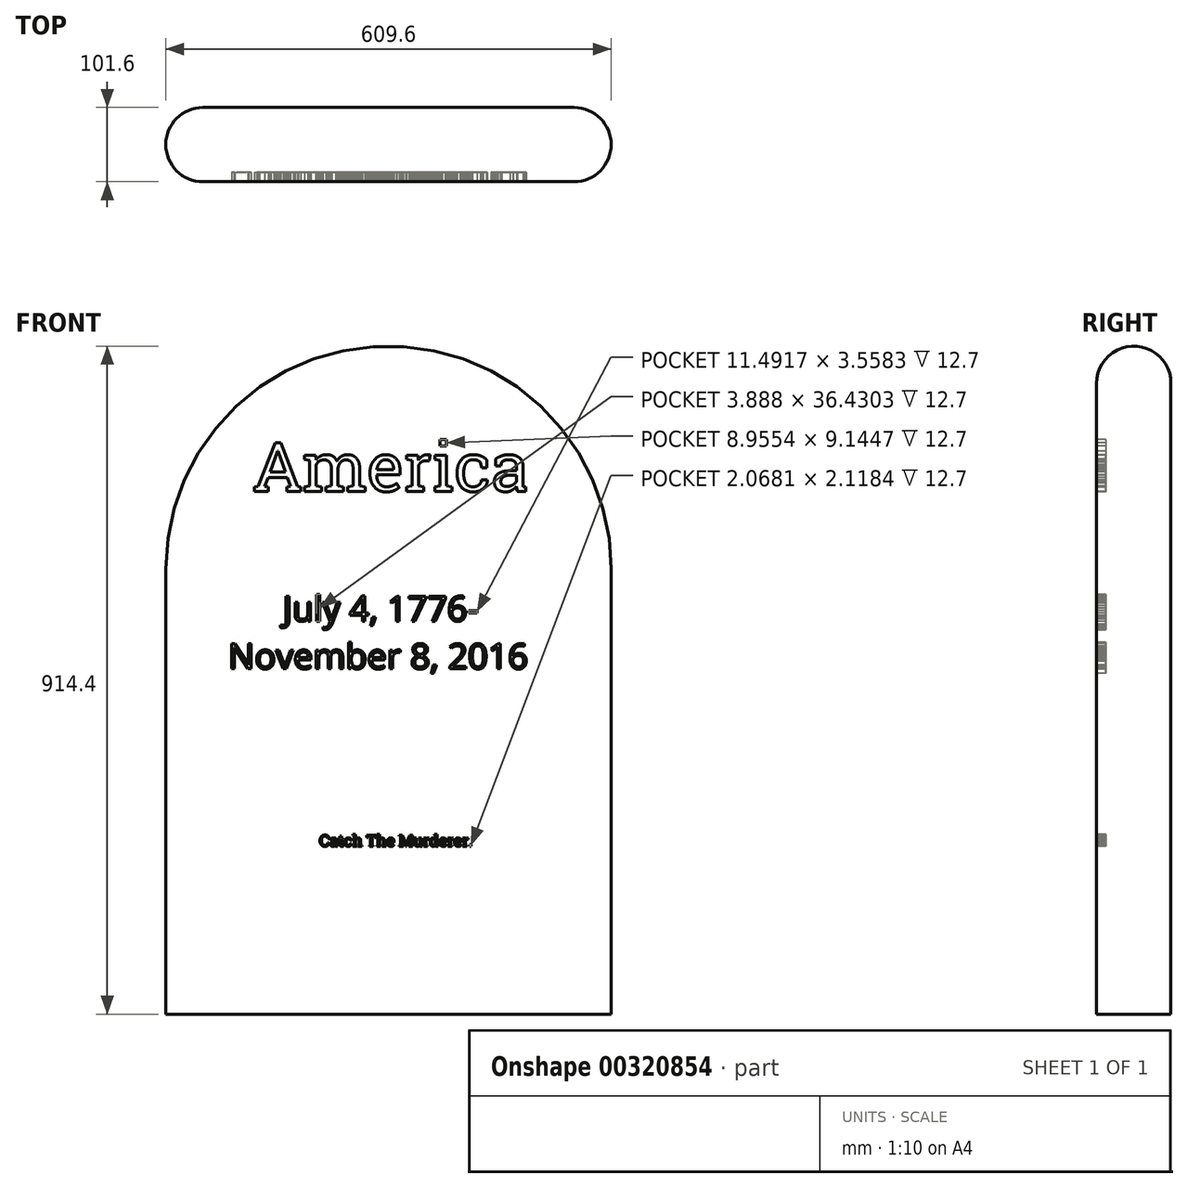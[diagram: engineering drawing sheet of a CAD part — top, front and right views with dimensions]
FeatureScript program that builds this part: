
annotation { "Feature Type Name" : "Feature", "Feature Type Description" : "" }
export const myFeature = defineFeature(function(context is Context, id is Id, definition is map)
    precondition{}
    {
        {
            var Q0;
            Q0=qCreatedBy(makeId("Front.planeOp"),FACE);
            var sketch = newSketch(context, id + "F0", { "sketchPlane" : qUnion([Q0])});
            skLineSegment(sketch, "E0.bottom", {"start": v(0, 0) * mm, "end": v(609.6, 0) * mm});
            skLineSegment(sketch, "E0.left", {"start": v(0, 0) * mm, "end": v(0, 609.6) * mm});
            skLineSegment(sketch, "E0.right", {"start": v(609.6, 0) * mm, "end": v(609.6, 609.6) * mm});
            skArc(sketch, "E1", {"start": v(609.6, 609.6) * mm, "mid": v(304.8, 914.4) * mm, "end": v(0, 609.6) * mm});
            skSolve(sketch);
        }
        {
            var Q0;
            Q0 = qSketchRegion(id + "F0", true);
            extrude(context, id + "F1", {"entities" : qUnion([Q0]), "depth" : 101.6 * mm});
        }
        {
            var Q0;
            Q0=makeQuery(id+"F1.opExtrude","CAP_EDGE",EDGE,{"disambiguationData":[OSD([sQuery(id+"F0.wireOp",EDGE,"E1")])],"isStart":false});
            var Q1;
            Q1=makeQuery(id+"F1.opExtrude","CAP_EDGE",EDGE,{"disambiguationData":[OSD([sQuery(id+"F0.wireOp",EDGE,"E1")])],"isStart":true});
            fillet(context, id + "F2", {"entities" : qUnion([Q0, Q1]), "radius" : 50.8 * mm, "tangentPropagation" : true, "allowEdgeOverflow" : false});
        }
        {
            var Q0;
            Q0=makeQuery(id+"F1.opExtrude","CAP_FACE",FACE,{"disambiguationData":[OSD([sQuery(id+"F0.wireOp",EDGE,"E0.bottom"),sQuery(id+"F0.wireOp",EDGE,"E0.left"),sQuery(id+"F0.wireOp",EDGE,"E0.right"),sQuery(id+"F0.wireOp",EDGE,"E1")])],"isStart":false});
            var sketch = newSketch(context, id + "F3", { "sketchPlane" : qUnion([Q0])});
            skText(sketch, "E2", { "text": "America", "fontName": "RobotoSlab-Regular.ttf"});
            skText(sketch, "E3", { "text": "      July 4, 1776-\nNovember 8, 2016", "fontName": "OpenSans-Regular.ttf"});
            skText(sketch, "E4", { "text": "Catch The Murderer.", "fontName": "RobotoSlab-Regular.ttf"});
            const initialGuessF3  = {"E2": [0.11902, 0.71571, 1, 0, 0.0671], "E3": [0.0855, 0.5378, 1, 0, 0.03452], "E4": [0.21017, 0.22974, 1, 0, 0.01547]};
            skSetInitialGuess(sketch, initialGuessF3);
            skSolve(sketch);
        }
        {
            var Q0;
            Q0 = qSketchRegion(id + "F3", true);
            extrude(context, id + "F4", {"entities" : qUnion([Q0]), "operationType" : NewBodyOperationType.REMOVE, "oppositeDirection" : true, "depth" : 12.7 * mm});
        }
    });
